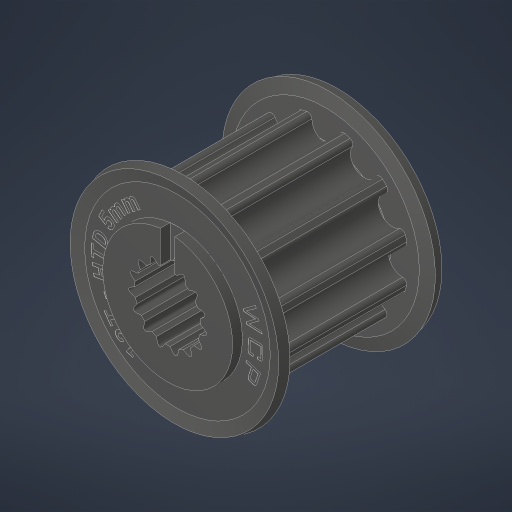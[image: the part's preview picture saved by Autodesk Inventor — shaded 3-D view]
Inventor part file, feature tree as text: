
AUTODESK INVENTOR PART (.ipt)
format: ipt  version: 2023.3 (Build 273359000, 359)  size: 651,264 bytes
history: native  units: in
note: dims shown in document units (in); Inventor stores cm internally (conversion verified against a paired STEP export)
features: other x2, mirror x1
ambient origin geometry x8: Origin, YZ Plane, XZ Plane, XY Plane, X Axis, Y Axis, Z Axis, Center Point
bodies: Solid1 (feature_tree), Solid2 (feature_tree), Solid3 (feature_tree)
feature tree (3):
  mirror  "Mirror2"
  other  "Cut-Extrude1"
  other  "Cut-Extrude2"
